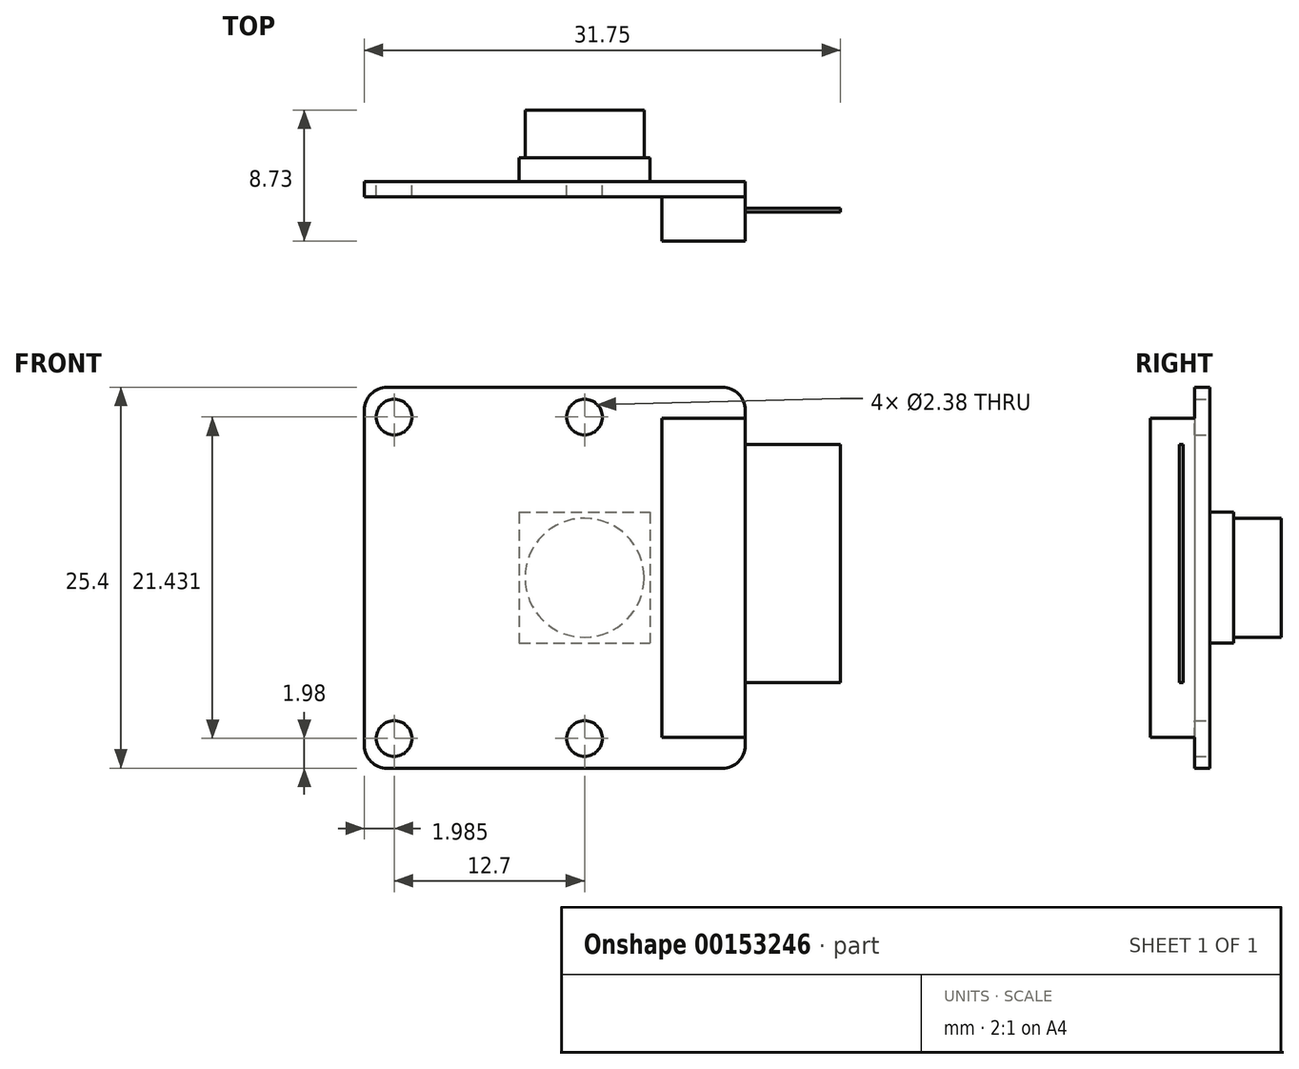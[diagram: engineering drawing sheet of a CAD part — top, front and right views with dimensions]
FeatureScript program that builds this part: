
annotation { "Feature Type Name" : "Feature", "Feature Type Description" : "" }
export const myFeature = defineFeature(function(context is Context, id is Id, definition is map)
    precondition{}
    {
        {
            var Q0;
            Q0=qCreatedBy(makeId("Front.planeOp"),FACE);
            var sketch = newSketch(context, id + "F0", { "sketchPlane" : qUnion([Q0])});
            skLineSegment(sketch, "E0.bottom", {"start": v(13.54, 11.75) * mm, "end": v(-11.86, 11.75) * mm});
            skLineSegment(sketch, "E0.top", {"start": v(13.54, -13.65) * mm, "end": v(-11.86, -13.65) * mm});
            skLineSegment(sketch, "E0.left", {"start": v(13.54, 11.75) * mm, "end": v(13.54, -13.65) * mm});
            skLineSegment(sketch, "E0.right", {"start": v(-11.86, 11.75) * mm, "end": v(-11.86, -13.65) * mm});
            skLineSegment(sketch, "E1", {"start": v(-9.88, 11.75) * mm, "end": v(-9.88, -13.65) * mm, "construction": true});
            skLineSegment(sketch, "E2", {"start": v(-11.86, -0.95) * mm, "end": v(13.54, -0.95) * mm, "construction": true});
            skCircle(sketch, "E3", {"center": v(-9.88, 9.76) * mm, "radius": 1.2 * mm});
            skCircle(sketch, "E4", {"center": v(-9.88, -11.67) * mm, "radius": 1.2 * mm});
            skLineSegment(sketch, "E5", {"start": v(2.82, 11.75) * mm, "end": v(2.82, -13.65) * mm, "construction": true});
            skCircle(sketch, "E6", {"center": v(2.82, 9.76) * mm, "radius": 1.2 * mm});
            skCircle(sketch, "E7", {"center": v(2.82, -11.67) * mm, "radius": 1.2 * mm});
            skCircle(sketch, "E8", {"center": v(2.82, -0.95) * mm, "radius": 3.97 * mm});
            skLineSegment(sketch, "E9.bottom", {"start": v(-1.54, 3.41) * mm, "end": v(7.2, 3.41) * mm});
            skLineSegment(sketch, "E9.top", {"start": v(-1.54, -5.32) * mm, "end": v(7.2, -5.32) * mm});
            skLineSegment(sketch, "E9.left", {"start": v(-1.54, 3.41) * mm, "end": v(-1.54, -5.32) * mm});
            skLineSegment(sketch, "E9.right", {"start": v(7.2, 3.41) * mm, "end": v(7.2, -5.32) * mm});
            skCircle(sketch, "E10", {"center": v(2.82, 15.28) * mm, "radius": 1.5 * mm});
            skSolve(sketch);
        }
        {
            var Q0;
            Q0=makeQuery(id+"F0.imprint","IMPRINT",FACE,{"disambiguationData":[TD([[makeQuery(id+"F0.imprint","IMPRINT",EDGE,{"derivedFrom":sQuery(id+"F0.wireOp",EDGE,"E0.bottom")}),1.0]])]});
            var Q1;
            Q1=makeQuery(id+"F0.imprint","IMPRINT",FACE,{"disambiguationData":[TD([[makeQuery(id+"F0.imprint","IMPRINT",EDGE,{"derivedFrom":sQuery(id+"F0.wireOp",EDGE,"E8")}),-1.0]])]});
            var Q2;
            Q2=makeQuery(id+"F0.imprint","IMPRINT",FACE,{"disambiguationData":[TD([[makeQuery(id+"F0.imprint","IMPRINT",EDGE,{"derivedFrom":sQuery(id+"F0.wireOp",EDGE,"E8")}),1.0]])]});
            extrude(context, id + "F1", {"entities" : qUnion([Q0, Q1, Q2]), "depth" : 1.02 * mm});
        }
        {
            var Q0;
            Q0=makeQuery(id+"F0.imprint","IMPRINT",FACE,{"disambiguationData":[TD([[makeQuery(id+"F0.imprint","IMPRINT",EDGE,{"derivedFrom":sQuery(id+"F0.wireOp",EDGE,"E8")}),-1.0]])]});
            var Q1;
            Q1=makeQuery(id+"F0.imprint","IMPRINT",FACE,{"disambiguationData":[TD([[makeQuery(id+"F0.imprint","IMPRINT",EDGE,{"derivedFrom":sQuery(id+"F0.wireOp",EDGE,"E8")}),1.0]])]});
            extrude(context, id + "F2", {"entities" : qUnion([Q0, Q1]), "operationType" : NewBodyOperationType.ADD, "oppositeDirection" : true, "depth" : 1.59 * mm});
        }
        {
            var Q0;
            Q0=makeQuery(id+"F0.imprint","IMPRINT",FACE,{"disambiguationData":[TD([[makeQuery(id+"F0.imprint","IMPRINT",EDGE,{"derivedFrom":sQuery(id+"F0.wireOp",EDGE,"E8")}),1.0]])]});
            extrude(context, id + "F3", {"entities" : qUnion([Q0]), "operationType" : NewBodyOperationType.ADD, "oppositeDirection" : true, "depth" : 4.76 * mm});
        }
        {
            var Q0;
            Q0=makeQuery(id+"F1.opExtrude","SWEPT_EDGE",EDGE,{"disambiguationData":[OSD([sQuery(id+"F0.wireOp",EDGE,"E0.bottom"),sQuery(id+"F0.wireOp",EDGE,"E0.right")])]});
            var Q1;
            Q1=makeQuery(id+"F1.opExtrude","SWEPT_EDGE",EDGE,{"disambiguationData":[OSD([sQuery(id+"F0.wireOp",EDGE,"E0.top"),sQuery(id+"F0.wireOp",EDGE,"E0.right")])]});
            var Q2;
            Q2=makeQuery(id+"F1.opExtrude","SWEPT_EDGE",EDGE,{"disambiguationData":[OSD([sQuery(id+"F0.wireOp",EDGE,"E0.top"),sQuery(id+"F0.wireOp",EDGE,"E0.left")])]});
            var Q3;
            Q3=makeQuery(id+"F1.opExtrude","SWEPT_EDGE",EDGE,{"disambiguationData":[OSD([sQuery(id+"F0.wireOp",EDGE,"E0.bottom"),sQuery(id+"F0.wireOp",EDGE,"E0.left")])]});
            fillet(context, id + "F4", {"entities" : qUnion([Q0, Q1, Q2, Q3]), "radius" : 1.52 * mm, "tangentPropagation" : true, "allowEdgeOverflow" : false});
        }
        {
            var Q0;
            Q0=makeQuery(id+"F1.opExtrude","CAP_FACE",FACE,{"disambiguationData":[OSD([sQuery(id+"F0.wireOp",EDGE,"E0.bottom"),sQuery(id+"F0.wireOp",EDGE,"E0.top"),sQuery(id+"F0.wireOp",EDGE,"E0.left"),sQuery(id+"F0.wireOp",EDGE,"E0.right"),sQuery(id+"F0.wireOp",EDGE,"E3"),sQuery(id+"F0.wireOp",EDGE,"E4"),sQuery(id+"F0.wireOp",EDGE,"E6"),sQuery(id+"F0.wireOp",EDGE,"E7")])],"isStart":false});
            var sketch = newSketch(context, id + "F5", { "sketchPlane" : qUnion([Q0])});
            skLineSegment(sketch, "E11.bottom", {"start": v(7.98, 9.69) * mm, "end": v(13.54, 9.69) * mm});
            skLineSegment(sketch, "E11.top", {"start": v(7.98, -11.6) * mm, "end": v(13.54, -11.6) * mm});
            skLineSegment(sketch, "E11.left", {"start": v(7.98, 9.69) * mm, "end": v(7.98, -11.6) * mm});
            skLineSegment(sketch, "E11.right", {"start": v(13.54, 9.69) * mm, "end": v(13.54, -11.6) * mm});
            skLineSegment(sketch, "E12", {"start": v(-11.86, -0.95) * mm, "end": v(42.66, -0.95) * mm, "construction": true});
            skPoint(sketch, "E12.endSnap0", {"position": v(-11.86, -0.95) * mm});
            skSolve(sketch);
        }
        {
            var Q0;
            Q0 = qSketchRegion(id + "F5", true);
            extrude(context, id + "F6", {"entities" : qUnion([Q0]), "operationType" : NewBodyOperationType.ADD, "depth" : 2.95 * mm});
        }
        {
            var Q0;
            Q0=makeQuery(id+"F6.boolean.opBoolean","MERGE",FACE,{"derivedFrom":[makeQuery(id+"F1.opExtrude","SWEPT_FACE",FACE,{"disambiguationData":[OSD([sQuery(id+"F0.wireOp",EDGE,"E0.left")])]}),makeQuery(id+"F6.opExtrude","SWEPT_FACE",FACE,{"disambiguationData":[OSD([sQuery(id+"F5.wireOp",EDGE,"E11.right")])]})]});
            var sketch = newSketch(context, id + "F7", { "sketchPlane" : qUnion([Q0])});
            skLineSegment(sketch, "E13", {"start": v(0, 0) * mm, "end": v(-13.8, 0) * mm, "construction": true});
            skLineSegment(sketch, "E14.bottom", {"start": v(-2.03, 7.94) * mm, "end": v(-1.78, 7.94) * mm});
            skLineSegment(sketch, "E14.top", {"start": v(-2.03, -7.94) * mm, "end": v(-1.78, -7.94) * mm});
            skLineSegment(sketch, "E14.left", {"start": v(-2.03, 7.94) * mm, "end": v(-2.03, -7.94) * mm});
            skLineSegment(sketch, "E14.right", {"start": v(-1.78, 7.94) * mm, "end": v(-1.78, -7.94) * mm});
            skSolve(sketch);
        }
        {
            var Q0;
            Q0 = qSketchRegion(id + "F7", true);
            extrude(context, id + "F8", {"entities" : qUnion([Q0]), "operationType" : NewBodyOperationType.ADD, "depth" : 6.35 * mm});
        }
    });
